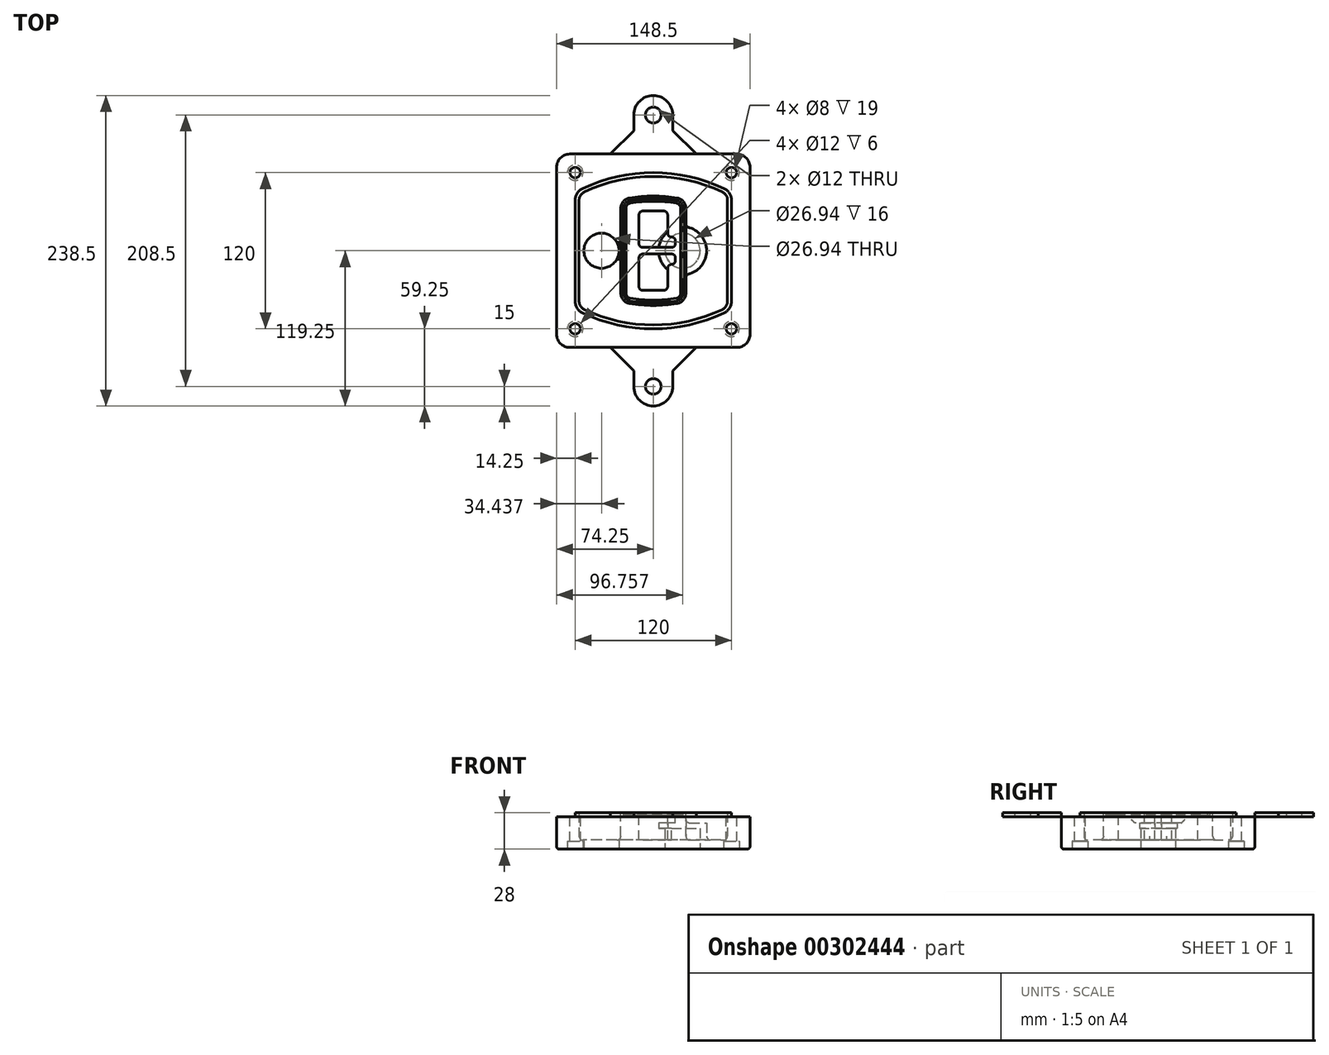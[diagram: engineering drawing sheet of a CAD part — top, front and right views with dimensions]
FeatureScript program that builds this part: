
annotation { "Feature Type Name" : "Feature", "Feature Type Description" : "" }
export const myFeature = defineFeature(function(context is Context, id is Id, definition is map)
    precondition{}
    {
        {
            var Q0;
            Q0=qCreatedBy(makeId("Top.planeOp"),FACE);
            var sketch = newSketch(context, id + "F0", { "sketchPlane" : qUnion([Q0])});
            skPoint(sketch, "E0.rect.middle", {"position": v(0, 0) * mm});
            skLineSegment(sketch, "E1.bottom", {"start": v(-64.25, -74.25) * mm, "end": v(64.25, -74.25) * mm});
            skLineSegment(sketch, "E1.top", {"start": v(-64.25, 74.25) * mm, "end": v(64.25, 74.25) * mm});
            skLineSegment(sketch, "E1.left", {"start": v(-74.25, -64.25) * mm, "end": v(-74.25, 64.25) * mm});
            skLineSegment(sketch, "E1.right", {"start": v(74.25, -64.25) * mm, "end": v(74.25, 64.25) * mm});
            skLineSegment(sketch, "E2", {"start": v(-74.25, 74.25) * mm, "end": v(74.25, -74.25) * mm, "construction": true});
            skLineSegment(sketch, "E3", {"start": v(74.25, 74.25) * mm, "end": v(-74.25, -74.25) * mm, "construction": true});
            skCircle(sketch, "E4", {"center": v(-60, 60) * mm, "radius": 4 * mm});
            skCircle(sketch, "E5", {"center": v(60, 60) * mm, "radius": 4 * mm});
            skCircle(sketch, "E6", {"center": v(60, -60) * mm, "radius": 4 * mm});
            skCircle(sketch, "E7", {"center": v(-60, -60) * mm, "radius": 4 * mm});
            skLineSegment(sketch, "E8", {"start": v(-60, 60) * mm, "end": v(60, 60) * mm, "construction": true});
            skLineSegment(sketch, "E9", {"start": v(60, 60) * mm, "end": v(60, -60) * mm, "construction": true});
            skLineSegment(sketch, "E10", {"start": v(60, -60) * mm, "end": v(-60, -60) * mm, "construction": true});
            skLineSegment(sketch, "E11", {"start": v(-60, -60) * mm, "end": v(-60, 60) * mm, "construction": true});
            skLineSegment(sketch, "E12", {"start": v(-60, 38.83) * mm, "end": v(-60, -38.83) * mm});
            skLineSegment(sketch, "E13", {"start": v(60, 38.83) * mm, "end": v(60, -38.83) * mm});
            skArc(sketch, "E14", {"start": v(54.26, 47.88) * mm, "mid": v(0, 60) * mm, "end": v(-54.26, 47.88) * mm});
            skArc(sketch, "E15", {"start": v(-54.26, -47.88) * mm, "mid": v(0, -60) * mm, "end": v(54.26, -47.88) * mm});
            skLineSegment(sketch, "E16", {"start": v(-60, 0) * mm, "end": v(60, 0) * mm, "construction": true});
            skPoint(sketch, "E17.visualSharp", {"position": v(-60, -45) * mm});
            skArc(sketch, "E17.filletArc", {"start": v(-60, -38.83) * mm, "mid": v(-58.44, -44.2) * mm, "end": v(-54.26, -47.88) * mm});
            skPoint(sketch, "E18.visualSharp", {"position": v(-60, 45) * mm});
            skArc(sketch, "E18.filletArc", {"start": v(-54.26, 47.88) * mm, "mid": v(-58.44, 44.2) * mm, "end": v(-60, 38.83) * mm});
            skPoint(sketch, "E19.visualSharp", {"position": v(60, 45) * mm});
            skArc(sketch, "E19.filletArc", {"start": v(60, 38.83) * mm, "mid": v(58.44, 44.2) * mm, "end": v(54.26, 47.88) * mm});
            skPoint(sketch, "E20.visualSharp", {"position": v(60, -45) * mm});
            skArc(sketch, "E20.filletArc", {"start": v(54.26, -47.88) * mm, "mid": v(58.44, -44.2) * mm, "end": v(60, -38.83) * mm});
            skPoint(sketch, "E21.visualSharp", {"position": v(-74.25, 74.25) * mm});
            skArc(sketch, "E21.filletArc", {"start": v(-64.25, 74.25) * mm, "mid": v(-71.32, 71.32) * mm, "end": v(-74.25, 64.25) * mm});
            skPoint(sketch, "E22.visualSharp", {"position": v(74.25, 74.25) * mm});
            skArc(sketch, "E22.filletArc", {"start": v(74.25, 64.25) * mm, "mid": v(71.32, 71.32) * mm, "end": v(64.25, 74.25) * mm});
            skPoint(sketch, "E23.visualSharp", {"position": v(74.25, -74.25) * mm});
            skArc(sketch, "E23.filletArc", {"start": v(64.25, -74.25) * mm, "mid": v(71.32, -71.32) * mm, "end": v(74.25, -64.25) * mm});
            skPoint(sketch, "E24.visualSharp", {"position": v(-74.25, -74.25) * mm});
            skArc(sketch, "E24.filletArc", {"start": v(-74.25, -64.25) * mm, "mid": v(-71.32, -71.32) * mm, "end": v(-64.25, -74.25) * mm});
            skArc(sketch, "E25.0", {"start": v(57, 38.83) * mm, "mid": v(55.9, 42.58) * mm, "end": v(52.98, 45.17) * mm});
            skLineSegment(sketch, "E25.1", {"start": v(57, 38.83) * mm, "end": v(57, -38.83) * mm});
            skArc(sketch, "E25.2", {"start": v(52.98, -45.17) * mm, "mid": v(55.9, -42.58) * mm, "end": v(57, -38.83) * mm});
            skArc(sketch, "E25.3", {"start": v(-52.98, -45.17) * mm, "mid": v(0, -57) * mm, "end": v(52.98, -45.17) * mm});
            skArc(sketch, "E25.4", {"start": v(-57, -38.83) * mm, "mid": v(-55.9, -42.58) * mm, "end": v(-52.98, -45.17) * mm});
            skArc(sketch, "E25.5", {"start": v(52.98, 45.17) * mm, "mid": v(0, 57) * mm, "end": v(-52.98, 45.17) * mm});
            skLineSegment(sketch, "E25.6", {"start": v(-57, 38.83) * mm, "end": v(-57, -38.83) * mm});
            skArc(sketch, "E25.7", {"start": v(-52.98, 45.17) * mm, "mid": v(-55.9, 42.58) * mm, "end": v(-57, 38.83) * mm});
            skArc(sketch, "E26.0", {"start": v(-55.96, 51.5) * mm, "mid": v(-61.82, 46.33) * mm, "end": v(-64, 38.83) * mm});
            skArc(sketch, "E26.1", {"start": v(55.96, 51.5) * mm, "mid": v(0, 64) * mm, "end": v(-55.96, 51.5) * mm});
            skArc(sketch, "E26.2", {"start": v(64, 38.83) * mm, "mid": v(61.82, 46.33) * mm, "end": v(55.96, 51.5) * mm});
            skLineSegment(sketch, "E26.3", {"start": v(64, 38.83) * mm, "end": v(64, -38.83) * mm});
            skArc(sketch, "E26.4", {"start": v(55.96, -51.5) * mm, "mid": v(61.82, -46.33) * mm, "end": v(64, -38.83) * mm});
            skLineSegment(sketch, "E26.5", {"start": v(-64, 38.83) * mm, "end": v(-64, -38.83) * mm});
            skArc(sketch, "E26.6", {"start": v(-55.96, -51.5) * mm, "mid": v(0, -64) * mm, "end": v(55.96, -51.5) * mm});
            skArc(sketch, "E26.7", {"start": v(-64, -38.83) * mm, "mid": v(-61.82, -46.33) * mm, "end": v(-55.96, -51.5) * mm});
            skSolve(sketch);
        }
        {
            var Q0;
            Q0=makeQuery(id+"F0.imprint","IMPRINT",FACE,{"disambiguationData":[TD([[makeQuery(id+"F0.imprint","IMPRINT",EDGE,{"derivedFrom":sQuery(id+"F0.wireOp",EDGE,"E1.bottom")}),1.0]])]});
            var Q1;
            Q1=makeQuery(id+"F0.imprint","IMPRINT",FACE,{"disambiguationData":[TD([[makeQuery(id+"F0.imprint","IMPRINT",EDGE,{"derivedFrom":sQuery(id+"F0.wireOp",EDGE,"E12")}),1.0]])]});
            var Q2;
            Q2=makeQuery(id+"F0.imprint","IMPRINT",FACE,{"disambiguationData":[TD([[makeQuery(id+"F0.imprint","IMPRINT",EDGE,{"derivedFrom":sQuery(id+"F0.wireOp",EDGE,"E25.0")}),1.0]])]});
            var Q3;
            Q3=makeQuery(id+"F0.imprint","IMPRINT",FACE,{"disambiguationData":[TD([[makeQuery(id+"F0.imprint","IMPRINT",EDGE,{"derivedFrom":sQuery(id+"F0.wireOp",EDGE,"E12")}),-1.0]])]});
            extrude(context, id + "F1", {"entities" : qUnion([Q0, Q1, Q2, Q3]), "oppositeDirection" : true, "depth" : 25 * mm});
        }
        {
            var Q0;
            Q0=makeQuery(id+"F0.imprint","IMPRINT",FACE,{"disambiguationData":[TD([[makeQuery(id+"F0.imprint","IMPRINT",EDGE,{"derivedFrom":sQuery(id+"F0.wireOp",EDGE,"E12")}),1.0]])]});
            extrude(context, id + "F2", {"entities" : qUnion([Q0]), "operationType" : NewBodyOperationType.ADD, "depth" : 3 * mm});
        }
        {
            var Q0;
            Q0=makeQuery(id+"F0.imprint","IMPRINT",FACE,{"disambiguationData":[TD([[makeQuery(id+"F0.imprint","IMPRINT",EDGE,{"derivedFrom":sQuery(id+"F0.wireOp",EDGE,"E25.0")}),1.0]])]});
            extrude(context, id + "F3", {"entities" : qUnion([Q0]), "operationType" : NewBodyOperationType.REMOVE, "oppositeDirection" : true, "depth" : 18 * mm});
        }
        {
            var Q0;
            Q0=makeQuery(id+"F2.opExtrude","CAP_FACE",FACE,{"disambiguationData":[OSD([sQuery(id+"F0.wireOp",EDGE,"E12"),sQuery(id+"F0.wireOp",EDGE,"E13"),sQuery(id+"F0.wireOp",EDGE,"E14"),sQuery(id+"F0.wireOp",EDGE,"E15"),sQuery(id+"F0.wireOp",EDGE,"E17.filletArc"),sQuery(id+"F0.wireOp",EDGE,"E18.filletArc"),sQuery(id+"F0.wireOp",EDGE,"E19.filletArc"),sQuery(id+"F0.wireOp",EDGE,"E20.filletArc"),sQuery(id+"F0.wireOp",EDGE,"E25.0"),sQuery(id+"F0.wireOp",EDGE,"E25.1"),sQuery(id+"F0.wireOp",EDGE,"E25.2"),sQuery(id+"F0.wireOp",EDGE,"E25.3"),sQuery(id+"F0.wireOp",EDGE,"E25.4"),sQuery(id+"F0.wireOp",EDGE,"E25.5"),sQuery(id+"F0.wireOp",EDGE,"E25.6"),sQuery(id+"F0.wireOp",EDGE,"E25.7")])],"isStart":false});
            var sketch = newSketch(context, id + "F4", { "sketchPlane" : qUnion([Q0])});
            skArc(sketch, "E27.0", {"start": v(-18.34, -40.45) * mm, "mid": v(0, -42) * mm, "end": v(18.34, -40.45) * mm});
            skArc(sketch, "E28.0", {"start": v(18.34, 40.45) * mm, "mid": v(0, 42) * mm, "end": v(-18.34, 40.45) * mm});
            skLineSegment(sketch, "E29", {"start": v(-25, 32.57) * mm, "end": v(-25, -32.57) * mm});
            skLineSegment(sketch, "E30", {"start": v(25, 32.57) * mm, "end": v(25, -32.57) * mm});
            skLineSegment(sketch, "E31", {"start": v(-25, 39.1) * mm, "end": v(25, 39.1) * mm, "construction": true});
            skLineSegment(sketch, "E32", {"start": v(-25, -39.1) * mm, "end": v(25, -39.1) * mm, "construction": true});
            skPoint(sketch, "E33.visualSharp", {"position": v(-25, 39.1) * mm});
            skArc(sketch, "E33.filletArc", {"start": v(-18.34, 40.45) * mm, "mid": v(-23.11, 37.73) * mm, "end": v(-25, 32.57) * mm});
            skPoint(sketch, "E34.visualSharp", {"position": v(25, 39.1) * mm});
            skArc(sketch, "E34.filletArc", {"start": v(25, 32.57) * mm, "mid": v(23.11, 37.73) * mm, "end": v(18.34, 40.45) * mm});
            skPoint(sketch, "E35.visualSharp", {"position": v(25, -39.1) * mm});
            skArc(sketch, "E35.filletArc", {"start": v(18.34, -40.45) * mm, "mid": v(23.11, -37.73) * mm, "end": v(25, -32.57) * mm});
            skPoint(sketch, "E36.visualSharp", {"position": v(-25, -39.1) * mm});
            skArc(sketch, "E36.filletArc", {"start": v(-25, -32.57) * mm, "mid": v(-23.11, -37.73) * mm, "end": v(-18.34, -40.45) * mm});
            skArc(sketch, "E37.0", {"start": v(52.98, 45.17) * mm, "mid": v(0, 57) * mm, "end": v(-52.98, 45.17) * mm});
            skArc(sketch, "E37.1", {"start": v(-52.98, 45.17) * mm, "mid": v(-55.9, 42.58) * mm, "end": v(-57, 38.83) * mm});
            skLineSegment(sketch, "E37.2", {"start": v(-57, 38.83) * mm, "end": v(-57, -38.83) * mm});
            skArc(sketch, "E37.3", {"start": v(-57, -38.83) * mm, "mid": v(-55.9, -42.58) * mm, "end": v(-52.98, -45.17) * mm});
            skArc(sketch, "E37.4", {"start": v(-52.98, -45.17) * mm, "mid": v(0, -57) * mm, "end": v(52.98, -45.17) * mm});
            skArc(sketch, "E37.5", {"start": v(52.98, -45.17) * mm, "mid": v(55.9, -42.58) * mm, "end": v(57, -38.83) * mm});
            skLineSegment(sketch, "E37.6", {"start": v(57, 38.83) * mm, "end": v(57, -38.83) * mm});
            skArc(sketch, "E37.7", {"start": v(57, 38.83) * mm, "mid": v(55.9, 42.58) * mm, "end": v(52.98, 45.17) * mm});
            skLineSegment(sketch, "E38.0", {"start": v(23, 32.57) * mm, "end": v(23, -32.57) * mm});
            skArc(sketch, "E38.1", {"start": v(18, -38.48) * mm, "mid": v(21.58, -36.44) * mm, "end": v(23, -32.57) * mm});
            skArc(sketch, "E38.2", {"start": v(-18, -38.48) * mm, "mid": v(0, -40) * mm, "end": v(18, -38.48) * mm});
            skArc(sketch, "E38.3", {"start": v(-23, -32.57) * mm, "mid": v(-21.58, -36.44) * mm, "end": v(-18, -38.48) * mm});
            skLineSegment(sketch, "E38.4", {"start": v(-23, 32.57) * mm, "end": v(-23, -32.57) * mm});
            skArc(sketch, "E38.5", {"start": v(23, 32.57) * mm, "mid": v(21.58, 36.44) * mm, "end": v(18, 38.48) * mm});
            skArc(sketch, "E38.6", {"start": v(-18, 38.48) * mm, "mid": v(-21.58, 36.44) * mm, "end": v(-23, 32.57) * mm});
            skArc(sketch, "E38.7", {"start": v(18, 38.48) * mm, "mid": v(0, 40) * mm, "end": v(-18, 38.48) * mm});
            skArc(sketch, "E39.0", {"start": v(21, 32.57) * mm, "mid": v(20.06, 35.15) * mm, "end": v(17.67, 36.5) * mm});
            skLineSegment(sketch, "E39.1", {"start": v(21, 32.57) * mm, "end": v(21, -32.57) * mm});
            skArc(sketch, "E39.2", {"start": v(17.67, -36.5) * mm, "mid": v(20.06, -35.15) * mm, "end": v(21, -32.57) * mm});
            skArc(sketch, "E39.3", {"start": v(-17.67, -36.5) * mm, "mid": v(0, -38) * mm, "end": v(17.67, -36.5) * mm});
            skArc(sketch, "E39.4", {"start": v(-21, -32.57) * mm, "mid": v(-20.06, -35.15) * mm, "end": v(-17.67, -36.5) * mm});
            skArc(sketch, "E39.5", {"start": v(17.67, 36.5) * mm, "mid": v(0, 38) * mm, "end": v(-17.67, 36.5) * mm});
            skLineSegment(sketch, "E39.6", {"start": v(-21, 32.57) * mm, "end": v(-21, -32.57) * mm});
            skArc(sketch, "E39.7", {"start": v(-17.67, 36.5) * mm, "mid": v(-20.06, 35.15) * mm, "end": v(-21, 32.57) * mm});
            skLineSegment(sketch, "E40", {"start": v(-25, 0) * mm, "end": v(25, 0) * mm, "construction": true});
            skLineSegment(sketch, "E41", {"start": v(-11, 5.5) * mm, "end": v(-11, 27.5) * mm});
            skLineSegment(sketch, "E42", {"start": v(-8, 30.5) * mm, "end": v(8, 30.5) * mm});
            skLineSegment(sketch, "E43", {"start": v(11, 27.5) * mm, "end": v(11, 13.5) * mm});
            skLineSegment(sketch, "E44", {"start": v(14, 10.5) * mm, "end": v(14, 10.5) * mm});
            skLineSegment(sketch, "E45", {"start": v(17, 7.5) * mm, "end": v(17, 5.5) * mm});
            skLineSegment(sketch, "E46", {"start": v(14, 2.5) * mm, "end": v(-8, 2.5) * mm});
            skPoint(sketch, "E47.visualSharp", {"position": v(-11, 30.5) * mm});
            skArc(sketch, "E47.filletArc", {"start": v(-8, 30.5) * mm, "mid": v(-10.12, 29.62) * mm, "end": v(-11, 27.5) * mm});
            skPoint(sketch, "E48.visualSharp", {"position": v(11, 30.5) * mm});
            skArc(sketch, "E48.filletArc", {"start": v(11, 27.5) * mm, "mid": v(10.12, 29.62) * mm, "end": v(8, 30.5) * mm});
            skPoint(sketch, "E49.visualSharp", {"position": v(11, 10.5) * mm});
            skArc(sketch, "E49.filletArc", {"start": v(11, 13.5) * mm, "mid": v(11.88, 11.38) * mm, "end": v(14, 10.5) * mm});
            skPoint(sketch, "E50.visualSharp", {"position": v(17, 10.5) * mm});
            skArc(sketch, "E50.filletArc", {"start": v(17, 7.5) * mm, "mid": v(16.12, 9.62) * mm, "end": v(14, 10.5) * mm});
            skPoint(sketch, "E51.visualSharp", {"position": v(17, 2.5) * mm});
            skArc(sketch, "E51.filletArc", {"start": v(14, 2.5) * mm, "mid": v(16.12, 3.38) * mm, "end": v(17, 5.5) * mm});
            skPoint(sketch, "E52.visualSharp", {"position": v(-11, 2.5) * mm});
            skArc(sketch, "E52.filletArc", {"start": v(-11, 5.5) * mm, "mid": v(-10.12, 3.38) * mm, "end": v(-8, 2.5) * mm});
            skLineSegment(sketch, "E53.0.MirrorCS", {"start": v(14, -2.5) * mm, "end": v(-8, -2.5) * mm});
            skArc(sketch, "E54.0.MirrorCS", {"start": v(-11, -5.5) * mm, "mid": v(-10.12, -3.38) * mm, "end": v(-8, -2.5) * mm});
            skLineSegment(sketch, "E55.0.MirrorCS", {"start": v(-11, -5.5) * mm, "end": v(-11, -27.5) * mm});
            skArc(sketch, "E56.0.MirrorCS", {"start": v(-8, -30.5) * mm, "mid": v(-10.12, -29.62) * mm, "end": v(-11, -27.5) * mm});
            skLineSegment(sketch, "E57.0.MirrorCS", {"start": v(-8, -30.5) * mm, "end": v(8, -30.5) * mm});
            skArc(sketch, "E58.0.MirrorCS", {"start": v(11, -27.5) * mm, "mid": v(10.12, -29.62) * mm, "end": v(8, -30.5) * mm});
            skLineSegment(sketch, "E59.0.MirrorCS", {"start": v(11, -27.5) * mm, "end": v(11, -13.5) * mm});
            skArc(sketch, "E60.0.MirrorCS", {"start": v(11, -13.5) * mm, "mid": v(11.88, -11.38) * mm, "end": v(14, -10.5) * mm});
            skArc(sketch, "E61.0.MirrorCS", {"start": v(17, -7.5) * mm, "mid": v(16.12, -9.62) * mm, "end": v(14, -10.5) * mm});
            skLineSegment(sketch, "E62.0.MirrorCS", {"start": v(17, -7.5) * mm, "end": v(17, -5.5) * mm});
            skArc(sketch, "E63.0.MirrorCS", {"start": v(14, -2.5) * mm, "mid": v(16.12, -3.38) * mm, "end": v(17, -5.5) * mm});
            skSolve(sketch);
        }
        {
            var Q0;
            Q0=makeQuery(id+"F4.imprint","IMPRINT",FACE,{"disambiguationData":[TD([[makeQuery(id+"F4.imprint","IMPRINT",EDGE,{"derivedFrom":sQuery(id+"F4.wireOp",EDGE,"E27.0")}),1.0]])]});
            var Q1;
            Q1=makeQuery(id+"F4.imprint","IMPRINT",FACE,{"disambiguationData":[TD([[makeQuery(id+"F4.imprint","IMPRINT",EDGE,{"derivedFrom":sQuery(id+"F4.wireOp",EDGE,"E38.0")}),-1.0]])]});
            var Q2;
            Q2=makeQuery(id+"F4.imprint","IMPRINT",FACE,{"disambiguationData":[TD([[makeQuery(id+"F4.imprint","IMPRINT",EDGE,{"derivedFrom":sQuery(id+"F4.wireOp",EDGE,"E39.0")}),1.0]])]});
            extrude(context, id + "F5", {"entities" : qUnion([Q0, Q1, Q2]), "operationType" : NewBodyOperationType.ADD, "endBound" : BoundingType.UP_TO_NEXT, "oppositeDirection" : true, "depth" : 25 * mm});
        }
        {
            var Q0;
            Q0=makeQuery(id+"F4.imprint","IMPRINT",FACE,{"disambiguationData":[TD([[makeQuery(id+"F4.imprint","IMPRINT",EDGE,{"derivedFrom":sQuery(id+"F4.wireOp",EDGE,"E38.0")}),-1.0]])]});
            extrude(context, id + "F6", {"entities" : qUnion([Q0]), "operationType" : NewBodyOperationType.REMOVE, "oppositeDirection" : true, "depth" : 2 * mm});
        }
        {
            var Q0;
            Q0=makeQuery(id+"F1.opExtrude","CAP_FACE",FACE,{"disambiguationData":[OSD([sQuery(id+"F0.wireOp",EDGE,"E1.bottom"),sQuery(id+"F0.wireOp",EDGE,"E1.top"),sQuery(id+"F0.wireOp",EDGE,"E1.left"),sQuery(id+"F0.wireOp",EDGE,"E1.right"),sQuery(id+"F0.wireOp",EDGE,"E4"),sQuery(id+"F0.wireOp",EDGE,"E5"),sQuery(id+"F0.wireOp",EDGE,"E6"),sQuery(id+"F0.wireOp",EDGE,"E7"),sQuery(id+"F0.wireOp",EDGE,"E21.filletArc"),sQuery(id+"F0.wireOp",EDGE,"E22.filletArc"),sQuery(id+"F0.wireOp",EDGE,"E23.filletArc"),sQuery(id+"F0.wireOp",EDGE,"E24.filletArc")])],"isStart":false});
            var sketch = newSketch(context, id + "F7", { "sketchPlane" : qUnion([Q0])});
            skCircle(sketch, "E64", {"center": v(22.5, 0) * mm, "radius": 13.47 * mm});
            skCircle(sketch, "E65", {"center": v(-39.81, 0) * mm, "radius": 13.47 * mm});
            skLineSegment(sketch, "E66", {"start": v(74.25, 0) * mm, "end": v(-74.25, 0) * mm});
            skCircle(sketch, "E67", {"center": v(22.5, 0) * mm, "radius": 18.47 * mm});
            skCircle(sketch, "E68", {"center": v(60, -60) * mm, "radius": 6 * mm});
            skCircle(sketch, "E69", {"center": v(-60, -60) * mm, "radius": 6 * mm});
            skCircle(sketch, "E70", {"center": v(-60, 60) * mm, "radius": 6 * mm});
            skCircle(sketch, "E71", {"center": v(60, 60) * mm, "radius": 6 * mm});
            skSolve(sketch);
        }
        {
            var Q0;
            {var subQ1=sQuery(id+"F7.wireOp",EDGE,"E66");var subQ4=sQuery(id+"F7.wireOp",EDGE,"E64");var subQ6=makeQuery(id+"F7.imprint","INTERSECT",VERTEX,{"disambiguationData":[OD(0.0)],"derivedFrom":[subQ4,subQ1]});Q0=makeQuery(id+"F7.imprint","IMPRINT",FACE,{"disambiguationData":[TD([[makeQuery(id+"F7.imprint","IMPRINT",EDGE,{"disambiguationData":[TD([[subQ6,-1.0]])],"derivedFrom":subQ4}),-1.0]])]});}
            var Q1;
            {var subQ0=sQuery(id+"F7.wireOp",EDGE,"E66");var subQ1=sQuery(id+"F7.wireOp",EDGE,"E64");var subQ3=makeQuery(id+"F7.imprint","INTERSECT",VERTEX,{"disambiguationData":[OD(0.0)],"derivedFrom":[subQ1,subQ0]});Q1=makeQuery(id+"F7.imprint","IMPRINT",FACE,{"disambiguationData":[TD([[makeQuery(id+"F7.imprint","IMPRINT",EDGE,{"disambiguationData":[TD([[subQ3,-1.0]])],"derivedFrom":subQ1}),1.0]])]});}
            var Q2;
            {var subQ0=sQuery(id+"F7.wireOp",EDGE,"E66");var subQ1=sQuery(id+"F7.wireOp",EDGE,"E64");var subQ3=makeQuery(id+"F7.imprint","INTERSECT",VERTEX,{"disambiguationData":[OD(0.0)],"derivedFrom":[subQ1,subQ0]});Q2=makeQuery(id+"F7.imprint","IMPRINT",FACE,{"disambiguationData":[TD([[makeQuery(id+"F7.imprint","IMPRINT",EDGE,{"disambiguationData":[TD([[subQ3,1.0]])],"derivedFrom":subQ1}),1.0]])]});}
            var Q3;
            {var subQ1=sQuery(id+"F7.wireOp",EDGE,"E66");var subQ4=sQuery(id+"F7.wireOp",EDGE,"E64");var subQ6=makeQuery(id+"F7.imprint","INTERSECT",VERTEX,{"disambiguationData":[OD(0.0)],"derivedFrom":[subQ4,subQ1]});Q3=makeQuery(id+"F7.imprint","IMPRINT",FACE,{"disambiguationData":[TD([[makeQuery(id+"F7.imprint","IMPRINT",EDGE,{"disambiguationData":[TD([[subQ6,1.0]])],"derivedFrom":subQ4}),-1.0]])]});}
            extrude(context, id + "F8", {"entities" : qUnion([Q0, Q1, Q2, Q3]), "operationType" : NewBodyOperationType.ADD, "oppositeDirection" : true, "depth" : 20 * mm});
        }
        {
            var Q0;
            {var subQ0=sQuery(id+"F7.wireOp",EDGE,"E66");var subQ1=sQuery(id+"F7.wireOp",EDGE,"E64");var subQ3=makeQuery(id+"F7.imprint","INTERSECT",VERTEX,{"disambiguationData":[OD(0.0)],"derivedFrom":[subQ1,subQ0]});Q0=makeQuery(id+"F7.imprint","IMPRINT",FACE,{"disambiguationData":[TD([[makeQuery(id+"F7.imprint","IMPRINT",EDGE,{"disambiguationData":[TD([[subQ3,-1.0]])],"derivedFrom":subQ1}),1.0]])]});}
            var Q1;
            {var subQ0=sQuery(id+"F7.wireOp",EDGE,"E66");var subQ1=sQuery(id+"F7.wireOp",EDGE,"E64");var subQ3=makeQuery(id+"F7.imprint","INTERSECT",VERTEX,{"disambiguationData":[OD(0.0)],"derivedFrom":[subQ1,subQ0]});Q1=makeQuery(id+"F7.imprint","IMPRINT",FACE,{"disambiguationData":[TD([[makeQuery(id+"F7.imprint","IMPRINT",EDGE,{"disambiguationData":[TD([[subQ3,1.0]])],"derivedFrom":subQ1}),1.0]])]});}
            extrude(context, id + "F9", {"entities" : qUnion([Q0, Q1]), "operationType" : NewBodyOperationType.REMOVE, "oppositeDirection" : true, "depth" : 16 * mm});
        }
        {
            var Q0;
            {var subQ0=sQuery(id+"F7.wireOp",EDGE,"E66");var subQ1=sQuery(id+"F7.wireOp",EDGE,"E65");var subQ3=makeQuery(id+"F7.imprint","INTERSECT",VERTEX,{"disambiguationData":[OD(0.0)],"derivedFrom":[subQ1,subQ0]});Q0=makeQuery(id+"F7.imprint","IMPRINT",FACE,{"disambiguationData":[TD([[makeQuery(id+"F7.imprint","IMPRINT",EDGE,{"disambiguationData":[TD([[subQ3,-1.0]])],"derivedFrom":subQ1}),1.0]])]});}
            var Q1;
            {var subQ0=sQuery(id+"F7.wireOp",EDGE,"E66");var subQ1=sQuery(id+"F7.wireOp",EDGE,"E65");var subQ3=makeQuery(id+"F7.imprint","INTERSECT",VERTEX,{"disambiguationData":[OD(0.0)],"derivedFrom":[subQ1,subQ0]});Q1=makeQuery(id+"F7.imprint","IMPRINT",FACE,{"disambiguationData":[TD([[makeQuery(id+"F7.imprint","IMPRINT",EDGE,{"disambiguationData":[TD([[subQ3,1.0]])],"derivedFrom":subQ1}),1.0]])]});}
            extrude(context, id + "F10", {"entities" : qUnion([Q0, Q1]), "operationType" : NewBodyOperationType.REMOVE, "oppositeDirection" : true, "depth" : 25 * mm});
        }
        {
            var Q0;
            Q0=makeQuery(id+"F7.imprint","IMPRINT",FACE,{"disambiguationData":[TD([[makeQuery(id+"F7.imprint","IMPRINT",EDGE,{"derivedFrom":sQuery(id+"F7.wireOp",EDGE,"E68")}),1.0]])]});
            var Q1;
            Q1=makeQuery(id+"F7.imprint","IMPRINT",FACE,{"disambiguationData":[TD([[makeQuery(id+"F7.imprint","IMPRINT",EDGE,{"derivedFrom":makeQuery(id+"F1.opExtrude","CAP_EDGE",EDGE,{"disambiguationData":[OSD([sQuery(id+"F0.wireOp",EDGE,"E5")])],"isStart":false})}),-1.0]])]});
            var Q2;
            Q2=makeQuery(id+"F7.imprint","IMPRINT",FACE,{"disambiguationData":[TD([[makeQuery(id+"F7.imprint","IMPRINT",EDGE,{"derivedFrom":sQuery(id+"F7.wireOp",EDGE,"E69")}),1.0]])]});
            var Q3;
            Q3=makeQuery(id+"F7.imprint","IMPRINT",FACE,{"disambiguationData":[TD([[makeQuery(id+"F7.imprint","IMPRINT",EDGE,{"derivedFrom":makeQuery(id+"F1.opExtrude","CAP_EDGE",EDGE,{"disambiguationData":[OSD([sQuery(id+"F0.wireOp",EDGE,"E4")])],"isStart":false})}),-1.0]])]});
            var Q4;
            Q4=makeQuery(id+"F7.imprint","IMPRINT",FACE,{"disambiguationData":[TD([[makeQuery(id+"F7.imprint","IMPRINT",EDGE,{"derivedFrom":sQuery(id+"F7.wireOp",EDGE,"E70")}),1.0]])]});
            var Q5;
            Q5=makeQuery(id+"F7.imprint","IMPRINT",FACE,{"disambiguationData":[TD([[makeQuery(id+"F7.imprint","IMPRINT",EDGE,{"derivedFrom":makeQuery(id+"F1.opExtrude","CAP_EDGE",EDGE,{"disambiguationData":[OSD([sQuery(id+"F0.wireOp",EDGE,"E7")])],"isStart":false})}),-1.0]])]});
            var Q6;
            Q6=makeQuery(id+"F7.imprint","IMPRINT",FACE,{"disambiguationData":[TD([[makeQuery(id+"F7.imprint","IMPRINT",EDGE,{"derivedFrom":sQuery(id+"F7.wireOp",EDGE,"E71")}),1.0]])]});
            var Q7;
            Q7=makeQuery(id+"F7.imprint","IMPRINT",FACE,{"disambiguationData":[TD([[makeQuery(id+"F7.imprint","IMPRINT",EDGE,{"derivedFrom":makeQuery(id+"F1.opExtrude","CAP_EDGE",EDGE,{"disambiguationData":[OSD([sQuery(id+"F0.wireOp",EDGE,"E6")])],"isStart":false})}),-1.0]])]});
            extrude(context, id + "F11", {"entities" : qUnion([Q0, Q1, Q2, Q3, Q4, Q5, Q6, Q7]), "operationType" : NewBodyOperationType.REMOVE, "oppositeDirection" : true, "depth" : 6 * mm});
        }
        {
            var Q0;
            Q0=makeQuery(id+"F9.boolean.opBoolean","COPY",FACE,{"derivedFrom":makeQuery(id+"F9.opExtrude","CAP_FACE",FACE,{"disambiguationData":[OSD([sQuery(id+"F7.wireOp",EDGE,"E64")])],"isStart":false})});
            var sketch = newSketch(context, id + "F12", { "sketchPlane" : qUnion([Q0])});
            skArc(sketch, "E72.0", {"start": v(11, 14.45) * mm, "mid": v(6.45, 9.13) * mm, "end": v(4.2, 2.5) * mm});
            skArc(sketch, "E72.1", {"start": v(4.2, -2.5) * mm, "mid": v(6.45, -9.13) * mm, "end": v(11, -14.45) * mm});
            skLineSegment(sketch, "E73", {"start": v(4.2, -2.5) * mm, "end": v(14, -2.5) * mm});
            skLineSegment(sketch, "E74.0", {"start": v(14, 2.5) * mm, "end": v(4.2, 2.5) * mm});
            skArc(sketch, "E74.1", {"start": v(14, 2.5) * mm, "mid": v(16.12, 3.38) * mm, "end": v(17, 5.5) * mm});
            skLineSegment(sketch, "E74.2", {"start": v(17, 7.5) * mm, "end": v(17, 5.5) * mm});
            skArc(sketch, "E74.3", {"start": v(17, 7.5) * mm, "mid": v(16.12, 9.62) * mm, "end": v(14, 10.5) * mm});
            skArc(sketch, "E74.4", {"start": v(11, 13.5) * mm, "mid": v(11.88, 11.38) * mm, "end": v(14, 10.5) * mm});
            skLineSegment(sketch, "E74.5", {"start": v(11, 14.45) * mm, "end": v(11, 13.5) * mm});
            skLineSegment(sketch, "E74.7", {"start": v(14, -2.5) * mm, "end": v(4.2, -2.5) * mm});
            skArc(sketch, "E74.8", {"start": v(14, -2.5) * mm, "mid": v(16.12, -3.38) * mm, "end": v(17, -5.5) * mm});
            skLineSegment(sketch, "E74.9", {"start": v(17, -7.5) * mm, "end": v(17, -5.5) * mm});
            skArc(sketch, "E74.10", {"start": v(17, -7.5) * mm, "mid": v(16.12, -9.62) * mm, "end": v(14, -10.5) * mm});
            skArc(sketch, "E74.11", {"start": v(11, -13.5) * mm, "mid": v(11.88, -11.38) * mm, "end": v(14, -10.5) * mm});
            skLineSegment(sketch, "E74.12", {"start": v(11, -14.45) * mm, "end": v(11, -13.5) * mm});
            skPoint(sketch, "E75.orphan", {"position": v(11, -27.5) * mm});
            skPoint(sketch, "E76.orphan", {"position": v(-8, -2.5) * mm});
            skPoint(sketch, "E77.orphan", {"position": v(-8, 2.5) * mm});
            skPoint(sketch, "E78.orphan", {"position": v(11, 27.5) * mm});
            skSolve(sketch);
        }
        {
            var Q0;
            {var subQ7=sQuery(id+"F12.wireOp",EDGE,"E72.0");var subQ14=sQuery(id+"F12.wireOp",EDGE,"E72.1");var subQ16=sQuery(id+"F12.wireOp",EDGE,"E74.1");var subQ18=sQuery(id+"F12.wireOp",EDGE,"E74.8");Q0=qUnion([makeQuery(id+"F12.imprint","IMPRINT",FACE,{"disambiguationData":[TD([[makeQuery(id+"F12.imprint","IMPRINT",EDGE,{"derivedFrom":subQ7}),1.0]])]}),makeQuery(id+"F12.imprint","IMPRINT",FACE,{"disambiguationData":[TD([[makeQuery(id+"F12.imprint","IMPRINT",EDGE,{"derivedFrom":subQ14}),1.0]])]}),makeQuery(id+"F12.imprint","IMPRINT",FACE,{"disambiguationData":[TD([[makeQuery(id+"F12.imprint","IMPRINT",EDGE,{"derivedFrom":subQ16}),1.0]])]}),makeQuery(id+"F12.imprint","IMPRINT",FACE,{"disambiguationData":[TD([[makeQuery(id+"F12.imprint","IMPRINT",EDGE,{"derivedFrom":subQ18}),-1.0]])]})]);}
            var Q1;
            Q1=makeQuery(id+"F5.boolean.opBoolean","SPLIT",FACE,{"disambiguationData":[TD([makeQuery(id+"F5.opExtrude","SWEPT_FACE",FACE,{"disambiguationData":[OSD([sQuery(id+"F4.wireOp",EDGE,"E41")])]})])],"derivedFrom":makeQuery(id+"F3.boolean.opBoolean","COPY",FACE,{"derivedFrom":makeQuery(id+"F3.opExtrude","CAP_FACE",FACE,{"disambiguationData":[OSD([sQuery(id+"F0.wireOp",EDGE,"E25.0"),sQuery(id+"F0.wireOp",EDGE,"E25.1"),sQuery(id+"F0.wireOp",EDGE,"E25.2"),sQuery(id+"F0.wireOp",EDGE,"E25.3"),sQuery(id+"F0.wireOp",EDGE,"E25.4"),sQuery(id+"F0.wireOp",EDGE,"E25.5"),sQuery(id+"F0.wireOp",EDGE,"E25.6"),sQuery(id+"F0.wireOp",EDGE,"E25.7")])],"isStart":false})})});
            extrude(context, id + "F13", {"entities" : qUnion([Q0]), "operationType" : NewBodyOperationType.REMOVE, "endBound" : BoundingType.UP_TO_SURFACE, "endBoundEntityFace" : qUnion([Q1]), "depth" : 25 * mm});
        }
        {
            var Q0;
            Q0=makeQuery(id+"F3.boolean.opBoolean","COPY",EDGE,{"derivedFrom":makeQuery(id+"F3.opExtrude","CAP_EDGE",EDGE,{"disambiguationData":[OSD([sQuery(id+"F0.wireOp",EDGE,"E25.6")])],"isStart":false})});
            var Q1;
            Q1=makeQuery(id+"F8.boolean.opBoolean","INTERSECT",EDGE,{"derivedFrom":[makeQuery(id+"F5.opExtrude","SWEPT_FACE",FACE,{"disambiguationData":[OSD([sQuery(id+"F4.wireOp",EDGE,"E30")])]}),makeQuery(id+"F8.opExtrude","CAP_FACE",FACE,{"disambiguationData":[OSD([sQuery(id+"F7.wireOp",EDGE,"E67")])],"isStart":false})]});
            var Q2;
            Q2=makeQuery(id+"F8.boolean.opBoolean","INTERSECT",EDGE,{"disambiguationData":[OD(1.0)],"derivedFrom":[makeQuery(id+"F5.opExtrude","SWEPT_FACE",FACE,{"disambiguationData":[OSD([sQuery(id+"F4.wireOp",EDGE,"E30")])]}),makeQuery(id+"F8.opExtrude","SWEPT_FACE",FACE,{"disambiguationData":[OSD([sQuery(id+"F7.wireOp",EDGE,"E67")])]})]});
            var Q3;
            {var subQ0=sQuery(id+"F4.wireOp",EDGE,"E30");Q3=makeQuery(id+"F8.boolean.opBoolean","SPLIT",EDGE,{"disambiguationData":[TD([makeQuery(id+"F5.opExtrude","SWEPT_FACE",FACE,{"disambiguationData":[OSD([sQuery(id+"F4.wireOp",EDGE,"E35.filletArc")])]})])],"derivedFrom":makeQuery(id+"F5.opExtrude","CAP_EDGE",EDGE,{"disambiguationData":[OSD([subQ0])],"isStart":false})});}
            var Q4;
            {var subQ0=sQuery(id+"F0.wireOp",EDGE,"E25.7");var subQ1=sQuery(id+"F0.wireOp",EDGE,"E25.1");var subQ2=sQuery(id+"F0.wireOp",EDGE,"E25.6");var subQ3=sQuery(id+"F0.wireOp",EDGE,"E25.5");var subQ4=sQuery(id+"F0.wireOp",EDGE,"E25.4");var subQ5=sQuery(id+"F0.wireOp",EDGE,"E25.0");var subQ6=sQuery(id+"F0.wireOp",EDGE,"E25.2");var subQ7=sQuery(id+"F0.wireOp",EDGE,"E25.3");Q4=makeQuery(id+"F8.boolean.opBoolean","INTERSECT",EDGE,{"derivedFrom":[makeQuery(id+"F5.boolean.opBoolean","SPLIT",FACE,{"disambiguationData":[TD([makeQuery(id+"F2.opExtrude","SWEPT_FACE",FACE,{"disambiguationData":[OSD([subQ5])]})])],"derivedFrom":makeQuery(id+"F3.boolean.opBoolean","COPY",FACE,{"derivedFrom":makeQuery(id+"F3.opExtrude","CAP_FACE",FACE,{"disambiguationData":[OSD([subQ5,subQ1,subQ6,subQ7,subQ4,subQ3,subQ2,subQ0])],"isStart":false})})}),makeQuery(id+"F8.opExtrude","SWEPT_FACE",FACE,{"disambiguationData":[OSD([sQuery(id+"F7.wireOp",EDGE,"E67")])]})]});}
            var Q5;
            Q5=makeQuery(id+"F8.boolean.opBoolean","INTERSECT",EDGE,{"disambiguationData":[OD(0.0)],"derivedFrom":[makeQuery(id+"F5.opExtrude","SWEPT_FACE",FACE,{"disambiguationData":[OSD([sQuery(id+"F4.wireOp",EDGE,"E30")])]}),makeQuery(id+"F8.opExtrude","SWEPT_FACE",FACE,{"disambiguationData":[OSD([sQuery(id+"F7.wireOp",EDGE,"E67")])]})]});
            fillet(context, id + "F14", {"entities" : qUnion([Q0, Q1, Q2, Q3, Q4, Q5]), "radius" : 3 * mm, "tangentPropagation" : true, "allowEdgeOverflow" : false});
        }
        {
            var Q0;
            Q0=makeQuery(id+"F1.opExtrude","CAP_EDGE",EDGE,{"disambiguationData":[OSD([sQuery(id+"F0.wireOp",EDGE,"E1.bottom")])],"isStart":false});
            fillet(context, id + "F15", {"entities" : qUnion([Q0]), "radius" : 2 * mm, "tangentPropagation" : true, "allowEdgeOverflow" : false});
        }
        {
            var Q0;
            {var subQ0=sQuery(id+"F0.wireOp",EDGE,"E21.filletArc");var subQ1=sQuery(id+"F0.wireOp",EDGE,"E7");var subQ2=sQuery(id+"F0.wireOp",EDGE,"E6");var subQ3=sQuery(id+"F0.wireOp",EDGE,"E5");var subQ4=sQuery(id+"F0.wireOp",EDGE,"E4");var subQ5=sQuery(id+"F0.wireOp",EDGE,"E22.filletArc");var subQ6=sQuery(id+"F0.wireOp",EDGE,"E1.bottom");var subQ7=sQuery(id+"F0.wireOp",EDGE,"E1.right");var subQ8=sQuery(id+"F0.wireOp",EDGE,"E1.top");var subQ9=sQuery(id+"F0.wireOp",EDGE,"E1.left");var subQ10=sQuery(id+"F0.wireOp",EDGE,"E23.filletArc");var subQ11=sQuery(id+"F0.wireOp",EDGE,"E24.filletArc");Q0=makeQuery(id+"F2.boolean.opBoolean","SPLIT",FACE,{"disambiguationData":[TD([makeQuery(id+"F1.opExtrude","SWEPT_FACE",FACE,{"disambiguationData":[OSD([subQ6])]})])],"derivedFrom":makeQuery(id+"F1.opExtrude","CAP_FACE",FACE,{"disambiguationData":[OSD([subQ6,subQ8,subQ9,subQ7,subQ4,subQ3,subQ2,subQ1,subQ0,subQ5,subQ10,subQ11])],"isStart":true})});}
            var sketch = newSketch(context, id + "F16", { "sketchPlane" : qUnion([Q0])});
            skLineSegment(sketch, "E79.0", {"start": v(-64.25, 74.25) * mm, "end": v(64.25, 74.25) * mm});
            skArc(sketch, "E79.1", {"start": v(-64.25, 74.25) * mm, "mid": v(-71.32, 71.32) * mm, "end": v(-74.25, 64.25) * mm});
            skLineSegment(sketch, "E79.2", {"start": v(-74.25, -64.25) * mm, "end": v(-74.25, 64.25) * mm});
            skArc(sketch, "E79.3", {"start": v(-74.25, -64.25) * mm, "mid": v(-71.32, -71.32) * mm, "end": v(-64.25, -74.25) * mm});
            skLineSegment(sketch, "E79.4", {"start": v(-64.25, -74.25) * mm, "end": v(64.25, -74.25) * mm});
            skArc(sketch, "E79.5", {"start": v(64.25, -74.25) * mm, "mid": v(71.32, -71.32) * mm, "end": v(74.25, -64.25) * mm});
            skLineSegment(sketch, "E79.6", {"start": v(74.25, -64.25) * mm, "end": v(74.25, 64.25) * mm});
            skArc(sketch, "E79.7", {"start": v(74.25, 64.25) * mm, "mid": v(71.32, 71.32) * mm, "end": v(64.25, 74.25) * mm});
            skArc(sketch, "E79.8", {"start": v(54.26, 47.88) * mm, "mid": v(0, 60) * mm, "end": v(-54.26, 47.88) * mm});
            skArc(sketch, "E79.9", {"start": v(60, 38.83) * mm, "mid": v(58.44, 44.2) * mm, "end": v(54.26, 47.88) * mm});
            skLineSegment(sketch, "E79.10", {"start": v(60, 38.83) * mm, "end": v(60, -38.83) * mm});
            skArc(sketch, "E79.11", {"start": v(54.26, -47.88) * mm, "mid": v(58.44, -44.2) * mm, "end": v(60, -38.83) * mm});
            skArc(sketch, "E79.12", {"start": v(-54.26, -47.88) * mm, "mid": v(0, -60) * mm, "end": v(54.26, -47.88) * mm});
            skArc(sketch, "E79.13", {"start": v(-60, -38.83) * mm, "mid": v(-58.44, -44.2) * mm, "end": v(-54.26, -47.88) * mm});
            skLineSegment(sketch, "E79.14", {"start": v(-60, 38.83) * mm, "end": v(-60, -38.83) * mm});
            skArc(sketch, "E79.15", {"start": v(-54.26, 47.88) * mm, "mid": v(-58.44, 44.2) * mm, "end": v(-60, 38.83) * mm});
            skLineSegment(sketch, "E80", {"start": v(0, 74.25) * mm, "end": v(0, 104.25) * mm, "construction": true});
            skCircle(sketch, "E81", {"center": v(0, 104.25) * mm, "radius": 6 * mm});
            skArc(sketch, "E82", {"start": v(15, 104.25) * mm, "mid": v(0, 119.25) * mm, "end": v(-15, 104.25) * mm});
            skLineSegment(sketch, "E83", {"start": v(-15, 104.25) * mm, "end": v(-15, 92.25) * mm});
            skLineSegment(sketch, "E84", {"start": v(-15, 92.25) * mm, "end": v(-33, 74.25) * mm});
            skLineSegment(sketch, "E85", {"start": v(15, 104.25) * mm, "end": v(15, 92.25) * mm});
            skLineSegment(sketch, "E86", {"start": v(15, 92.25) * mm, "end": v(33, 74.25) * mm});
            skLineSegment(sketch, "E87", {"start": v(-74.25, 0) * mm, "end": v(0, 0) * mm, "construction": true});
            skLineSegment(sketch, "E88", {"start": v(0, 0) * mm, "end": v(74.25, 0) * mm, "construction": true});
            skLineSegment(sketch, "E89.MirrorCS", {"start": v(-15, -92.25) * mm, "end": v(-33, -74.25) * mm});
            skLineSegment(sketch, "E90.MirrorCS", {"start": v(-15, -104.25) * mm, "end": v(-15, -92.25) * mm});
            skArc(sketch, "E91.MirrorCS", {"start": v(15, -104.25) * mm, "mid": v(0, -119.25) * mm, "end": v(-15, -104.25) * mm});
            skLineSegment(sketch, "E92.MirrorCS", {"start": v(15, -104.25) * mm, "end": v(15, -92.25) * mm});
            skLineSegment(sketch, "E93.MirrorCS", {"start": v(15, -92.25) * mm, "end": v(33, -74.25) * mm});
            skLineSegment(sketch, "E94.MirrorCS", {"start": v(0, -74.25) * mm, "end": v(0, -104.25) * mm, "construction": true});
            skCircle(sketch, "E95.MirrorC", {"center": v(0, -104.25) * mm, "radius": 6 * mm});
            skSolve(sketch);
        }
        {
            var Q0;
            Q0=makeQuery(id+"F16.imprint","IMPRINT",FACE,{"disambiguationData":[TD([[makeQuery(id+"F16.imprint","IMPRINT",EDGE,{"derivedFrom":sQuery(id+"F16.wireOp",EDGE,"E81")}),-1.0]])]});
            var Q1;
            {var subQ0=sQuery(id+"F16.wireOp",EDGE,"E89.MirrorCS");Q1=makeQuery(id+"F16.imprint","IMPRINT",FACE,{"disambiguationData":[TD([[makeQuery(id+"F16.imprint","IMPRINT",EDGE,{"derivedFrom":subQ0}),-1.0]])]});}
            var Q2;
            Q2=makeQuery(id+"F2.opExtrude","CAP_FACE",FACE,{"disambiguationData":[OSD([sQuery(id+"F0.wireOp",EDGE,"E12"),sQuery(id+"F0.wireOp",EDGE,"E13"),sQuery(id+"F0.wireOp",EDGE,"E14"),sQuery(id+"F0.wireOp",EDGE,"E15"),sQuery(id+"F0.wireOp",EDGE,"E17.filletArc"),sQuery(id+"F0.wireOp",EDGE,"E18.filletArc"),sQuery(id+"F0.wireOp",EDGE,"E19.filletArc"),sQuery(id+"F0.wireOp",EDGE,"E20.filletArc"),sQuery(id+"F0.wireOp",EDGE,"E25.0"),sQuery(id+"F0.wireOp",EDGE,"E25.1"),sQuery(id+"F0.wireOp",EDGE,"E25.2"),sQuery(id+"F0.wireOp",EDGE,"E25.3"),sQuery(id+"F0.wireOp",EDGE,"E25.4"),sQuery(id+"F0.wireOp",EDGE,"E25.5"),sQuery(id+"F0.wireOp",EDGE,"E25.6"),sQuery(id+"F0.wireOp",EDGE,"E25.7")])],"isStart":false});
            extrude(context, id + "F17", {"entities" : qUnion([Q0, Q1]), "endBound" : BoundingType.UP_TO_SURFACE, "endBoundEntityFace" : qUnion([Q2]), "depth" : 25 * mm});
        }
    });
